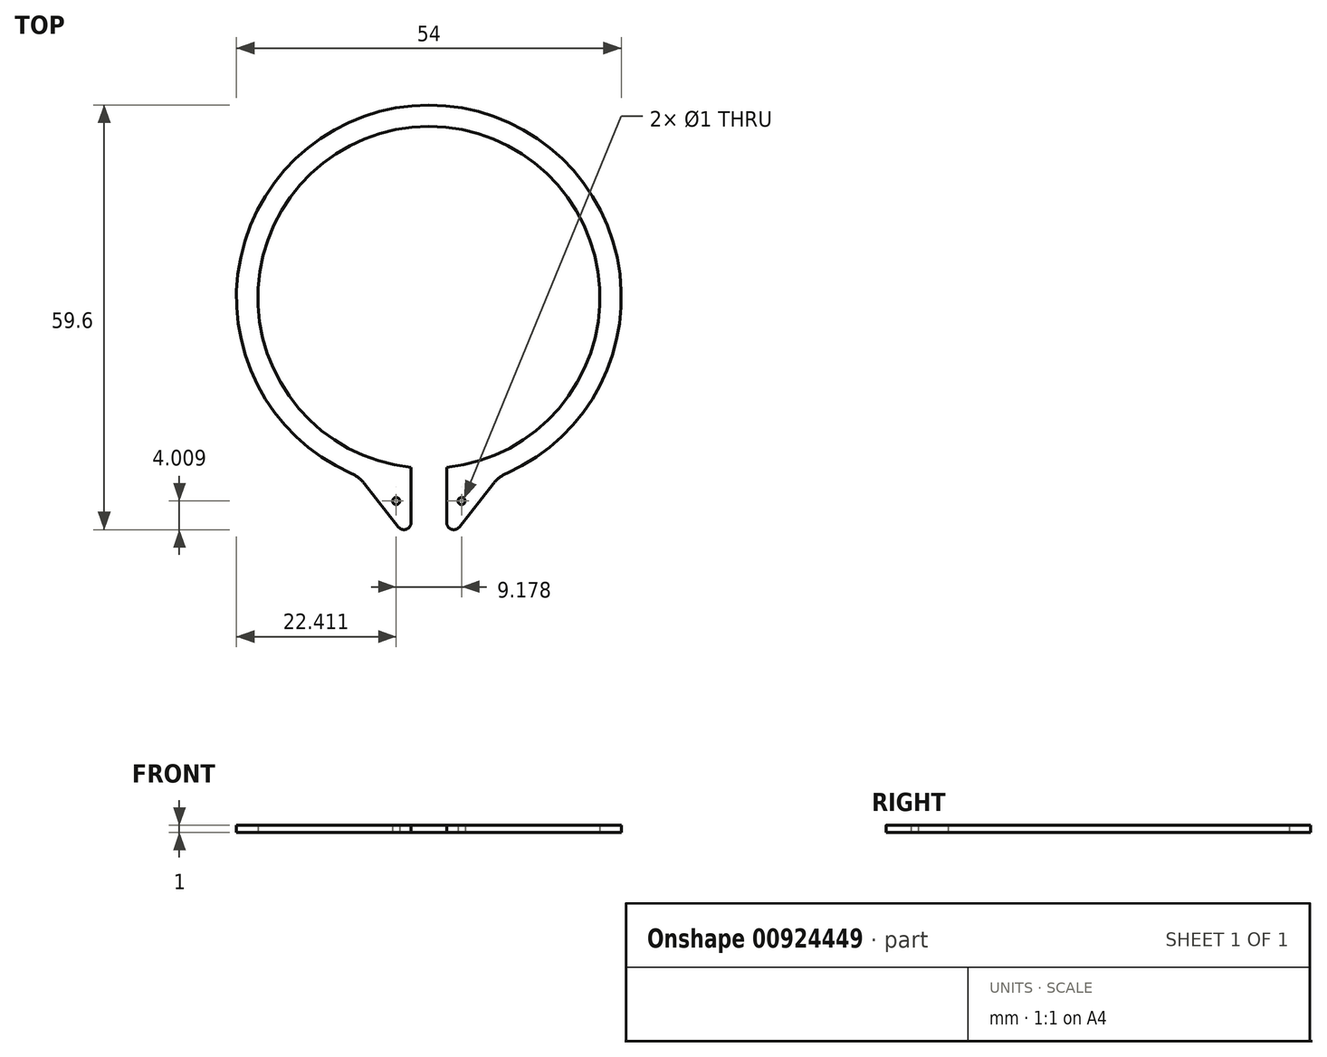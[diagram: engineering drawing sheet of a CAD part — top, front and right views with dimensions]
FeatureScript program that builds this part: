
annotation { "Feature Type Name" : "Feature", "Feature Type Description" : "" }
export const myFeature = defineFeature(function(context is Context, id is Id, definition is map)
    precondition{}
    {
        {
            var Q0;
            Q0=qCreatedBy(makeId("Top.planeOp"),FACE);
            var sketch = newSketch(context, id + "F0", { "sketchPlane" : qUnion([Q0])});
            skCircle(sketch, "E0", {"center": v(0, 0) * mm, "radius": 24 * mm});
            skCircle(sketch, "E1", {"center": v(0, 0) * mm, "radius": 27 * mm});
            skLineSegment(sketch, "E2", {"start": v(0, 0) * mm, "end": v(0, -27) * mm});
            skLineSegment(sketch, "E3.bottom", {"start": v(2.5, -19.5) * mm, "end": v(-2.5, -19.5) * mm});
            skLineSegment(sketch, "E3.top", {"start": v(2.5, -34.5) * mm, "end": v(-2.5, -34.5) * mm});
            skLineSegment(sketch, "E3.left", {"start": v(2.5, -19.5) * mm, "end": v(2.5, -34.5) * mm});
            skLineSegment(sketch, "E3.right", {"start": v(-2.5, -19.5) * mm, "end": v(-2.5, -34.5) * mm});
            skPoint(sketch, "E3.middle", {"position": v(0, -27) * mm});
            skLineSegment(sketch, "E4", {"start": v(9.83, -25.15) * mm, "end": v(0, -27) * mm});
            skLineSegment(sketch, "E5", {"start": v(0, -27) * mm, "end": v(-9.83, -25.15) * mm});
            skLineSegment(sketch, "E6", {"start": v(9.83, -25.15) * mm, "end": v(2.5, -34.5) * mm});
            skLineSegment(sketch, "E7", {"start": v(-2.5, -34.5) * mm, "end": v(-9.83, -25.15) * mm});
            skPoint(sketch, "E8", {"position": v(6.16, -29.82) * mm});
            skPoint(sketch, "E9", {"position": v(-6.16, -29.82) * mm});
            skLineSegment(sketch, "E10", {"start": v(6.16, -29.82) * mm, "end": v(4.59, -28.6) * mm});
            skLineSegment(sketch, "E11", {"start": v(-6.16, -29.82) * mm, "end": v(-4.59, -28.6) * mm});
            skSolve(sketch);
        }
        {
            var Q0;
            {var subQ0=sQuery(id+"F0.wireOp",EDGE,"E7");Q0=makeQuery(id+"F0.imprint","IMPRINT",FACE,{"disambiguationData":[TD([[makeQuery(id+"F0.imprint","IMPRINT",EDGE,{"derivedFrom":subQ0}),-1.0]])]});}
            var Q1;
            {var subQ0=sQuery(id+"F0.wireOp",EDGE,"E6");Q1=makeQuery(id+"F0.imprint","IMPRINT",FACE,{"disambiguationData":[TD([[makeQuery(id+"F0.imprint","IMPRINT",EDGE,{"derivedFrom":subQ0}),-1.0]])]});}
            var Q2;
            {var subQ1=sQuery(id+"F0.wireOp",EDGE,"E1");var subQ3=sQuery(id+"F0.wireOp",EDGE,"E3.right");var subQ4=makeQuery(id+"F0.imprint","INTERSECT",VERTEX,{"derivedFrom":[subQ1,subQ3]});Q2=makeQuery(id+"F0.imprint","IMPRINT",FACE,{"disambiguationData":[TD([[makeQuery(id+"F0.imprint","IMPRINT",EDGE,{"disambiguationData":[TD([[subQ4,1.0]])],"derivedFrom":subQ3}),-1.0]])]});}
            var Q3;
            {var subQ1=sQuery(id+"F0.wireOp",EDGE,"E1");var subQ3=sQuery(id+"F0.wireOp",EDGE,"E3.left");var subQ4=makeQuery(id+"F0.imprint","INTERSECT",VERTEX,{"derivedFrom":[subQ1,subQ3]});Q3=makeQuery(id+"F0.imprint","IMPRINT",FACE,{"disambiguationData":[TD([[makeQuery(id+"F0.imprint","IMPRINT",EDGE,{"disambiguationData":[TD([[subQ4,1.0]])],"derivedFrom":subQ3}),1.0]])]});}
            var Q4;
            {var subQ0=sQuery(id+"F0.wireOp",EDGE,"E3.right");var subQ1=sQuery(id+"F0.wireOp",EDGE,"E0");var subQ2=makeQuery(id+"F0.imprint","INTERSECT",VERTEX,{"derivedFrom":[subQ1,subQ0]});Q4=makeQuery(id+"F0.imprint","IMPRINT",FACE,{"disambiguationData":[TD([[makeQuery(id+"F0.imprint","IMPRINT",EDGE,{"disambiguationData":[TD([[subQ2,1.0]])],"derivedFrom":subQ1}),-1.0]])]});}
            extrude(context, id + "F1", {"entities" : qUnion([Q0, Q1, Q2, Q3, Q4]), "depth" : 1 * mm, "offsetDistance" : 25 * mm});
        }
        {
            var Q0;
            Q0=makeQuery(id+"F1.opExtrude","SWEPT_EDGE",EDGE,{"disambiguationData":[OSD([sQuery(id+"F0.wireOp",EDGE,"E3.top"),sQuery(id+"F0.wireOp",EDGE,"E3.left"),sQuery(id+"F0.wireOp",EDGE,"E6")])]});
            fillet(context, id + "F2", {"entities" : qUnion([Q0]), "radius" : 1 * mm, "tangentPropagation" : true, "allowEdgeOverflow" : false});
        }
        {
            var Q0;
            Q0=makeQuery(id+"F1.opExtrude","SWEPT_EDGE",EDGE,{"disambiguationData":[OSD([sQuery(id+"F0.wireOp",EDGE,"E3.top"),sQuery(id+"F0.wireOp",EDGE,"E3.right"),sQuery(id+"F0.wireOp",EDGE,"E7")])]});
            fillet(context, id + "F3", {"entities" : qUnion([Q0]), "radius" : 1 * mm, "tangentPropagation" : true, "allowEdgeOverflow" : false});
        }
        {
            var Q0;
            Q0=sQuery(id+"F0.wireOp",VERTEX,"E11.end");
            var Q1;
            Q1=sQuery(id+"F0.wireOp",VERTEX,"E10.end");
            var Q2;
            Q2=makeQuery(id+"F1.opExtrude","SWEPT_BODY",BODY,{"disambiguationData":[OSD([sQuery(id+"F0.wireOp",EDGE,"E0"),sQuery(id+"F0.wireOp",EDGE,"E1"),sQuery(id+"F0.wireOp",EDGE,"E3.left"),sQuery(id+"F0.wireOp",EDGE,"E3.right"),sQuery(id+"F0.wireOp",EDGE,"E6"),sQuery(id+"F0.wireOp",EDGE,"E7")])]});
            hole(context, id + "F4", {"style" : HoleStyle.SIMPLE, "endStyle" : HoleEndStyle.BLIND, "oppositeDirection" : true, "holeDiameter" : 1 * mm, "majorDiameter" : 5 * mm, "holeDepth" : 2 * mm, "isTappedThrough" : true, "tappedDepth" : 12 * mm, "tapClearance" : 3, "locations" : qUnion([Q0, Q1]), "scope" : qUnion([Q2])});
        }
        {
            var Q0;
            Q0=makeQuery(id+"F1.opExtrude","SWEPT_EDGE",EDGE,{"disambiguationData":[OSD([sQuery(id+"F0.wireOp",EDGE,"E1"),sQuery(id+"F0.wireOp",EDGE,"E5"),sQuery(id+"F0.wireOp",EDGE,"E7")])]});
            fillet(context, id + "F5", {"entities" : qUnion([Q0]), "radius" : 5 * mm, "tangentPropagation" : true, "allowEdgeOverflow" : false});
        }
        {
            var Q0;
            Q0=makeQuery(id+"F1.opExtrude","SWEPT_EDGE",EDGE,{"disambiguationData":[OSD([sQuery(id+"F0.wireOp",EDGE,"E1"),sQuery(id+"F0.wireOp",EDGE,"E4"),sQuery(id+"F0.wireOp",EDGE,"E6")])]});
            fillet(context, id + "F6", {"entities" : qUnion([Q0]), "radius" : 5 * mm, "tangentPropagation" : true, "allowEdgeOverflow" : false});
        }
    });
